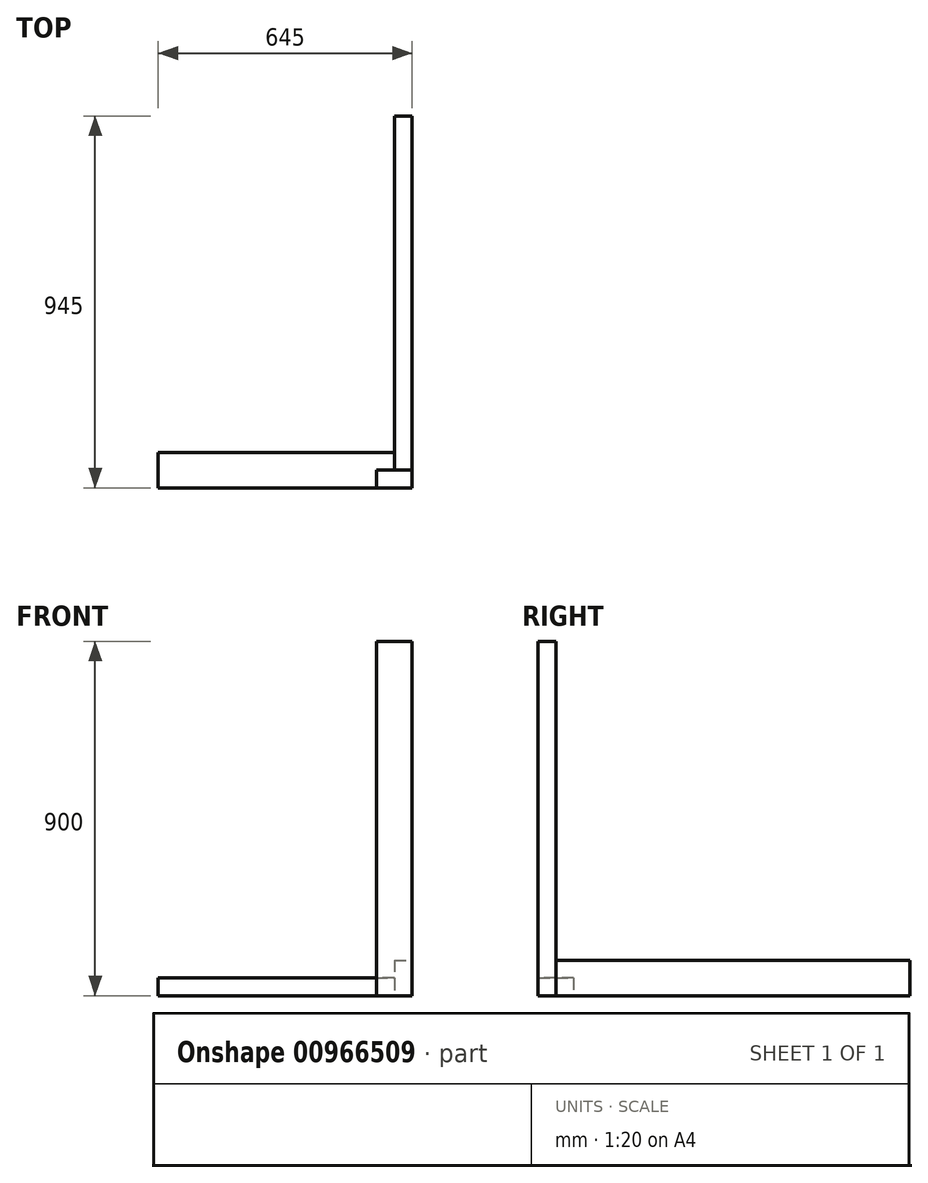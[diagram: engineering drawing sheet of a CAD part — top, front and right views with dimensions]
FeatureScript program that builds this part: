
annotation { "Feature Type Name" : "Feature", "Feature Type Description" : "" }
export const myFeature = defineFeature(function(context is Context, id is Id, definition is map)
    precondition{}
    {
        {
            var Q0;
            Q0=qCreatedBy(makeId("Top.planeOp"),FACE);
            var sketch = newSketch(context, id + "F0", { "sketchPlane" : qUnion([Q0])});
            skLineSegment(sketch, "E0.bottom", {"start": v(0, 0) * mm, "end": v(45, 0) * mm});
            skLineSegment(sketch, "E0.top", {"start": v(0, 900) * mm, "end": v(45, 900) * mm});
            skLineSegment(sketch, "E0.left", {"start": v(0, 0) * mm, "end": v(0, 900) * mm});
            skLineSegment(sketch, "E0.right", {"start": v(45, 0) * mm, "end": v(45, 900) * mm});
            skSolve(sketch);
        }
        {
            var Q0;
            Q0 = qSketchRegion(id + "F0", true);
            extrude(context, id + "F1", {"entities" : qUnion([Q0]), "depth" : 90 * mm, "offsetDistance" : 25 * mm});
        }
        {
            var Q0;
            Q0=qCreatedBy(makeId("Top.planeOp"),FACE);
            var sketch = newSketch(context, id + "F2", { "sketchPlane" : qUnion([Q0])});
            skLineSegment(sketch, "E1.bottom", {"start": v(45, 0) * mm, "end": v(-45, 0) * mm});
            skLineSegment(sketch, "E1.top", {"start": v(45, -45) * mm, "end": v(-45, -45) * mm});
            skLineSegment(sketch, "E1.left", {"start": v(45, 0) * mm, "end": v(45, -45) * mm});
            skLineSegment(sketch, "E1.right", {"start": v(-45, 0) * mm, "end": v(-45, -45) * mm});
            skSolve(sketch);
        }
        {
            var Q0;
            Q0 = qSketchRegion(id + "F2", true);
            extrude(context, id + "F3", {"entities" : qUnion([Q0]), "depth" : 900 * mm, "offsetDistance" : 25 * mm});
        }
        {
            var Q0;
            Q0=qCreatedBy(makeId("Top.planeOp"),FACE);
            var sketch = newSketch(context, id + "F4", { "sketchPlane" : qUnion([Q0])});
            skLineSegment(sketch, "E2", {"start": v(0, 45) * mm, "end": v(0, 0) * mm});
            skLineSegment(sketch, "E3", {"start": v(0, 0) * mm, "end": v(-45, 0) * mm});
            skLineSegment(sketch, "E4", {"start": v(-45, 0) * mm, "end": v(-45, -45) * mm});
            skLineSegment(sketch, "E5", {"start": v(-45, -45) * mm, "end": v(-600, -45) * mm});
            skLineSegment(sketch, "E6", {"start": v(-600, -45) * mm, "end": v(-600, 45) * mm});
            skLineSegment(sketch, "E7", {"start": v(-600, 45) * mm, "end": v(0, 45) * mm});
            skSolve(sketch);
        }
        {
            var Q0;
            Q0 = qSketchRegion(id + "F4", true);
            extrude(context, id + "F5", {"entities" : qUnion([Q0]), "depth" : 45 * mm, "offsetDistance" : 25 * mm});
        }
    });
